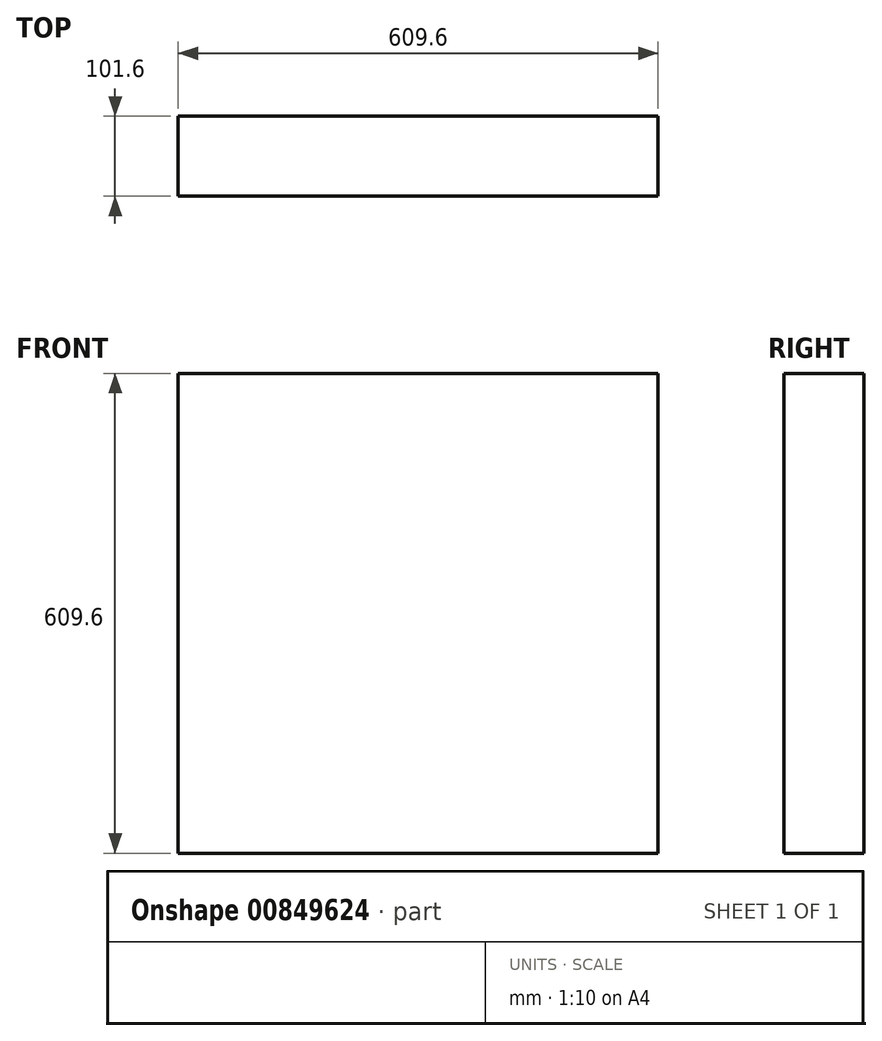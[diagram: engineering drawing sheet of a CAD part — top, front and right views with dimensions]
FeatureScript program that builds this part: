
annotation { "Feature Type Name" : "Feature", "Feature Type Description" : "" }
export const myFeature = defineFeature(function(context is Context, id is Id, definition is map)
    precondition{}
    {
        {
            var Q0;
            Q0=qCreatedBy(makeId("Front.planeOp"),FACE);
            var sketch = newSketch(context, id + "F0", { "sketchPlane" : qUnion([Q0])});
            skLineSegment(sketch, "E0.bottom", {"start": v(-365.07, 0) * mm, "end": v(244.53, 0) * mm});
            skLineSegment(sketch, "E0.top", {"start": v(-365.07, 609.6) * mm, "end": v(244.53, 609.6) * mm});
            skLineSegment(sketch, "E0.left", {"start": v(-365.07, 0) * mm, "end": v(-365.07, 609.6) * mm});
            skLineSegment(sketch, "E0.right", {"start": v(244.53, 0) * mm, "end": v(244.53, 609.6) * mm});
            skSolve(sketch);
        }
        {
            var Q0;
            Q0 = qSketchRegion(id + "F0", true);
            extrude(context, id + "F1", {"entities" : qUnion([Q0]), "depth" : 101.6 * mm, "offsetDistance" : 25.4 * mm});
        }
    });
